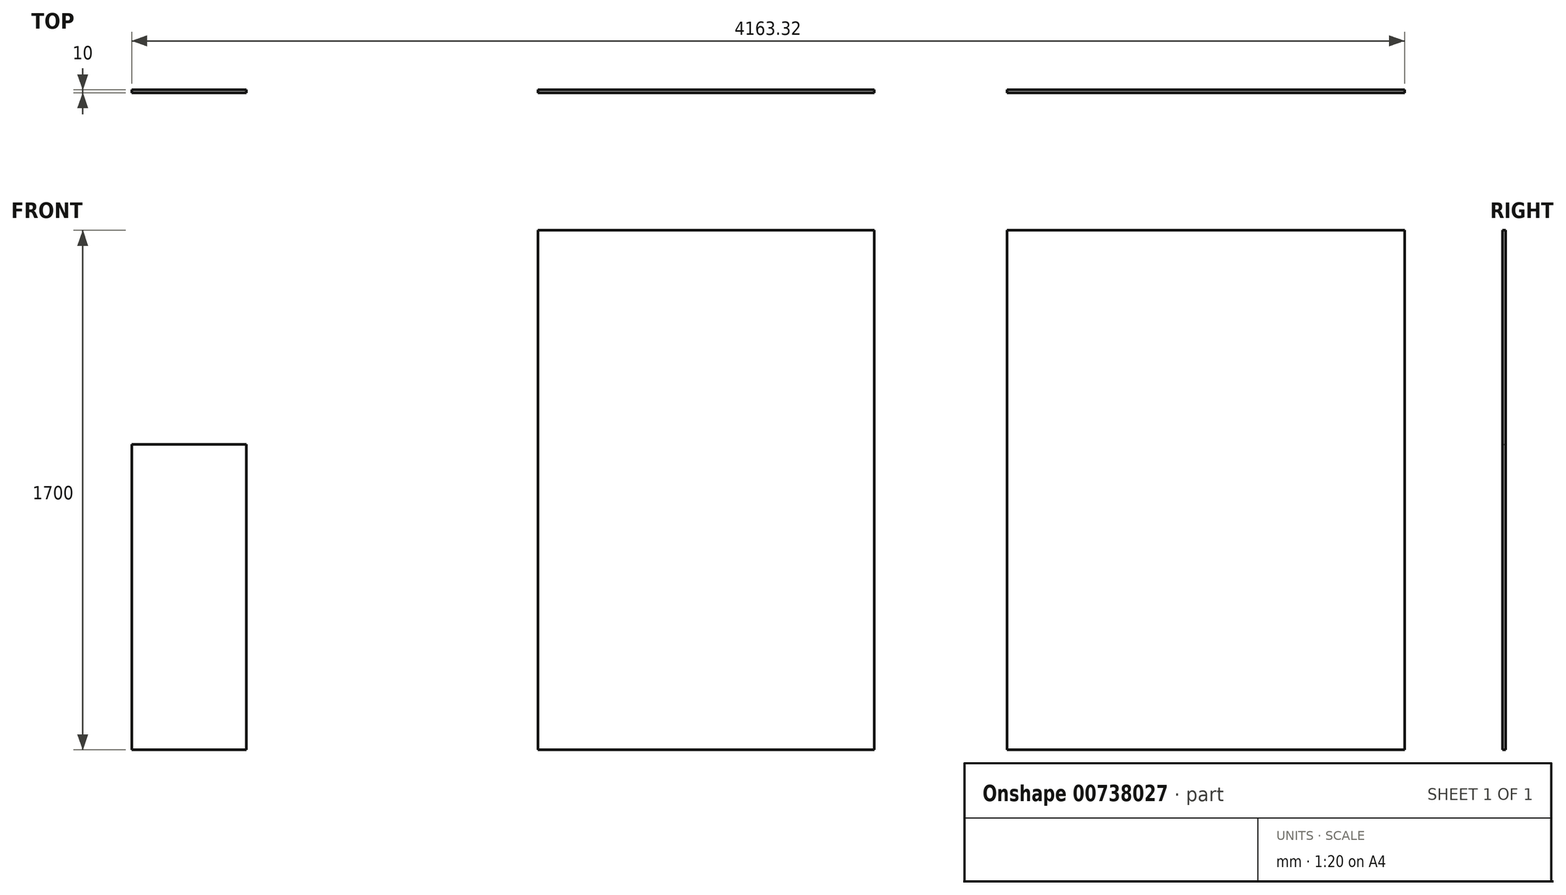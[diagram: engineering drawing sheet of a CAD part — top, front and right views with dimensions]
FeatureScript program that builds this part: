
annotation { "Feature Type Name" : "Feature", "Feature Type Description" : "" }
export const myFeature = defineFeature(function(context is Context, id is Id, definition is map)
    precondition{}
    {
        {
            var Q0;
            Q0=qCreatedBy(makeId("Front.planeOp"),FACE);
            var sketch = newSketch(context, id + "F0", { "sketchPlane" : qUnion([Q0])});
            skLineSegment(sketch, "E0.bottom", {"start": v(-72.94, 0) * mm, "end": v(1027.06, 0) * mm});
            skLineSegment(sketch, "E0.top", {"start": v(-72.94, 1700) * mm, "end": v(1027.06, 1700) * mm});
            skLineSegment(sketch, "E0.left", {"start": v(-72.94, 0) * mm, "end": v(-72.94, 1700) * mm});
            skLineSegment(sketch, "E0.right", {"start": v(1027.06, 0) * mm, "end": v(1027.06, 1700) * mm});
            skLineSegment(sketch, "E1.bottom", {"start": v(1461.63, 0) * mm, "end": v(2761.63, 0) * mm});
            skLineSegment(sketch, "E1.top", {"start": v(1461.63, 1700) * mm, "end": v(2761.63, 1700) * mm});
            skLineSegment(sketch, "E1.left", {"start": v(1461.63, 0) * mm, "end": v(1461.63, 1700) * mm});
            skLineSegment(sketch, "E1.right", {"start": v(2761.63, 0) * mm, "end": v(2761.63, 1700) * mm});
            skLineSegment(sketch, "E2.bottom", {"start": v(-1026.7, 0) * mm, "end": v(-1401.7, 0) * mm});
            skLineSegment(sketch, "E2.top", {"start": v(-1026.7, 1000) * mm, "end": v(-1401.7, 1000) * mm});
            skLineSegment(sketch, "E2.left", {"start": v(-1026.7, 0) * mm, "end": v(-1026.7, 1000) * mm});
            skLineSegment(sketch, "E2.right", {"start": v(-1401.7, 0) * mm, "end": v(-1401.7, 1000) * mm});
            skSolve(sketch);
        }
        {
            var Q0;
            Q0=qSketchRegion(id+"F0",true);
            extrude(context, id + "F1", {"entities" : qUnion([Q0]), "depth" : 10 * mm, "offsetDistance" : 25 * mm});
        }
    });
